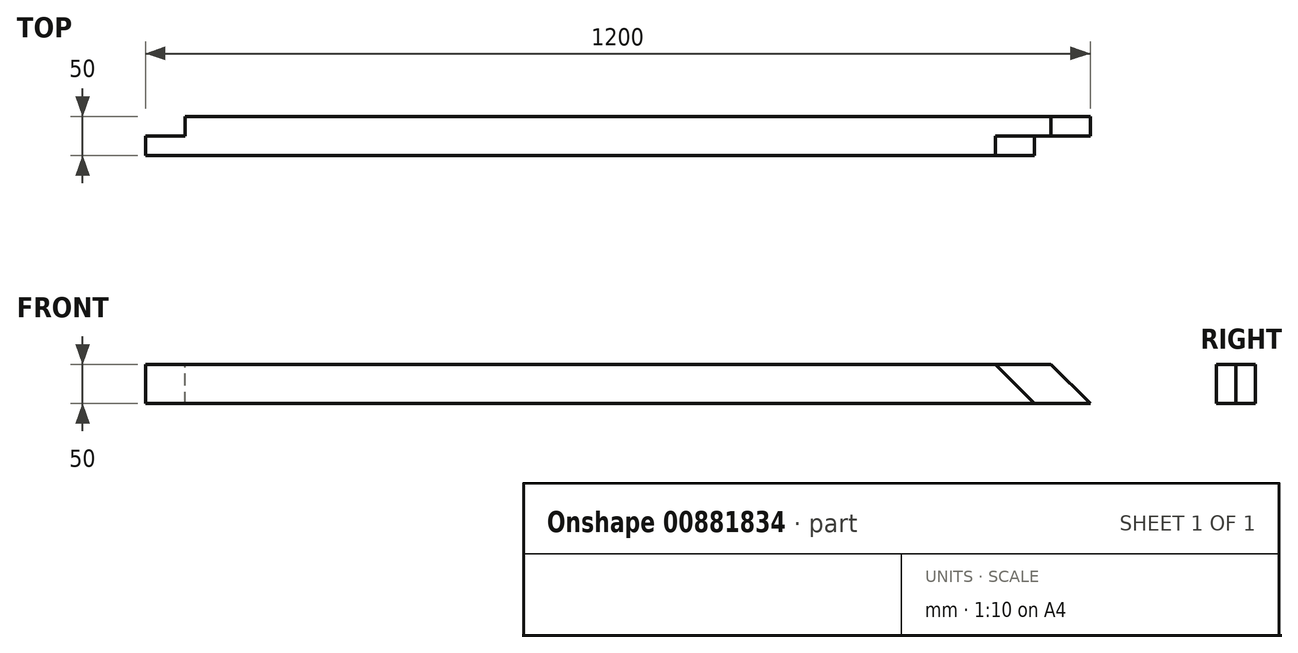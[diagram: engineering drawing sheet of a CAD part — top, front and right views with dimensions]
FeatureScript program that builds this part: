
annotation { "Feature Type Name" : "Feature", "Feature Type Description" : "" }
export const myFeature = defineFeature(function(context is Context, id is Id, definition is map)
    precondition{}
    {
        {
            var Q0;
            Q0=qCreatedBy(makeId("Front.planeOp"),FACE);
            var sketch = newSketch(context, id + "F0", { "sketchPlane" : qUnion([Q0])});
            skLineSegment(sketch, "E0", {"start": v(374.6, 24.7) * mm, "end": v(1574.6, 24.7) * mm});
            skLineSegment(sketch, "E1", {"start": v(1524.6, 74.7) * mm, "end": v(374.6, 74.7) * mm});
            skLineSegment(sketch, "E2", {"start": v(374.6, 74.7) * mm, "end": v(374.6, 24.7) * mm});
            skLineSegment(sketch, "E3", {"start": v(1574.6, 24.7) * mm, "end": v(1524.6, 74.7) * mm});
            skSolve(sketch);
        }
        {
            var Q0;
            Q0=qSketchRegion(id+"F0",true);
            extrude(context, id + "F1", {"entities" : qUnion([Q0]), "depth" : 50 * mm, "offsetDistance" : 25 * mm});
        }
        {
            var Q0;
            Q0=makeQuery(id+"F1.opExtrude","CAP_FACE",FACE,{"disambiguationData":[OSD([sQuery(id+"F0.wireOp",EDGE,"E0"),sQuery(id+"F0.wireOp",EDGE,"E1"),sQuery(id+"F0.wireOp",EDGE,"E2"),sQuery(id+"F0.wireOp",EDGE,"E3")])],"isStart":false});
            var sketch = newSketch(context, id + "F2", { "sketchPlane" : qUnion([Q0])});
            skLineSegment(sketch, "E4", {"start": v(1574.6, 24.7) * mm, "end": v(1524.6, 74.7) * mm});
            skLineSegment(sketch, "E5", {"start": v(1453.89, 74.7) * mm, "end": v(1503.89, 24.7) * mm});
            skLineSegment(sketch, "E6", {"start": v(1524.6, 74.7) * mm, "end": v(1453.89, 74.7) * mm});
            skLineSegment(sketch, "E7", {"start": v(1574.6, 24.7) * mm, "end": v(1503.89, 24.7) * mm});
            skSolve(sketch);
        }
        {
            var Q0;
            Q0 = qSketchRegion(id + "F2", true);
            extrude(context, id + "F3", {"entities" : qUnion([Q0]), "operationType" : NewBodyOperationType.REMOVE, "oppositeDirection" : true, "depth" : 25 * mm, "offsetDistance" : 25 * mm});
        }
        {
            var Q0;
            Q0=makeQuery(id+"F1.opExtrude","CAP_FACE",FACE,{"disambiguationData":[OSD([sQuery(id+"F0.wireOp",EDGE,"E0"),sQuery(id+"F0.wireOp",EDGE,"E1"),sQuery(id+"F0.wireOp",EDGE,"E2"),sQuery(id+"F0.wireOp",EDGE,"E3")])],"isStart":true});
            var sketch = newSketch(context, id + "F4", { "sketchPlane" : qUnion([Q0])});
            skLineSegment(sketch, "E8.bottom", {"start": v(-374.6, 24.7) * mm, "end": v(-424.6, 24.7) * mm});
            skLineSegment(sketch, "E8.top", {"start": v(-374.6, 74.7) * mm, "end": v(-424.6, 74.7) * mm});
            skLineSegment(sketch, "E8.left", {"start": v(-374.6, 24.7) * mm, "end": v(-374.6, 74.7) * mm});
            skLineSegment(sketch, "E8.right", {"start": v(-424.6, 24.7) * mm, "end": v(-424.6, 74.7) * mm});
            skSolve(sketch);
        }
        {
            var Q0;
            Q0 = qSketchRegion(id + "F4", true);
            extrude(context, id + "F5", {"entities" : qUnion([Q0]), "operationType" : NewBodyOperationType.REMOVE, "oppositeDirection" : true, "depth" : 25 * mm, "offsetDistance" : 25 * mm});
        }
    });
